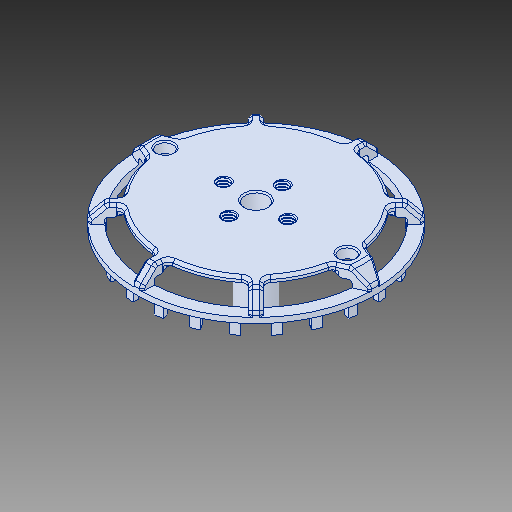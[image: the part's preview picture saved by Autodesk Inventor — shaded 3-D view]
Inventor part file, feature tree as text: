
AUTODESK INVENTOR PART (.ipt)
format: ipt  version: 2019.4 (Build 234330000, 330)  size: 1,063,424 bytes
history: mixed  units: mm
features: thread x1, imported_body x1
ambient origin geometry x8: Origin, YZ Plane, XZ Plane, XY Plane, X Axis, Y Axis, Z Axis, Center Point
bodies: Solid1 (imported_parasolid)
feature tree (2):
  thread  "Thread5"  [1 undecoded]
  imported_body  NMx_Import_Brep_tag  [imported B-rep: ~6 faces, bbox_mm=None]
note: 1 required parameter value undecoded (feature->parameter linkage not recoverable at this tier; creation-order binding heuristic only, values carry confidence <= 0.55)
